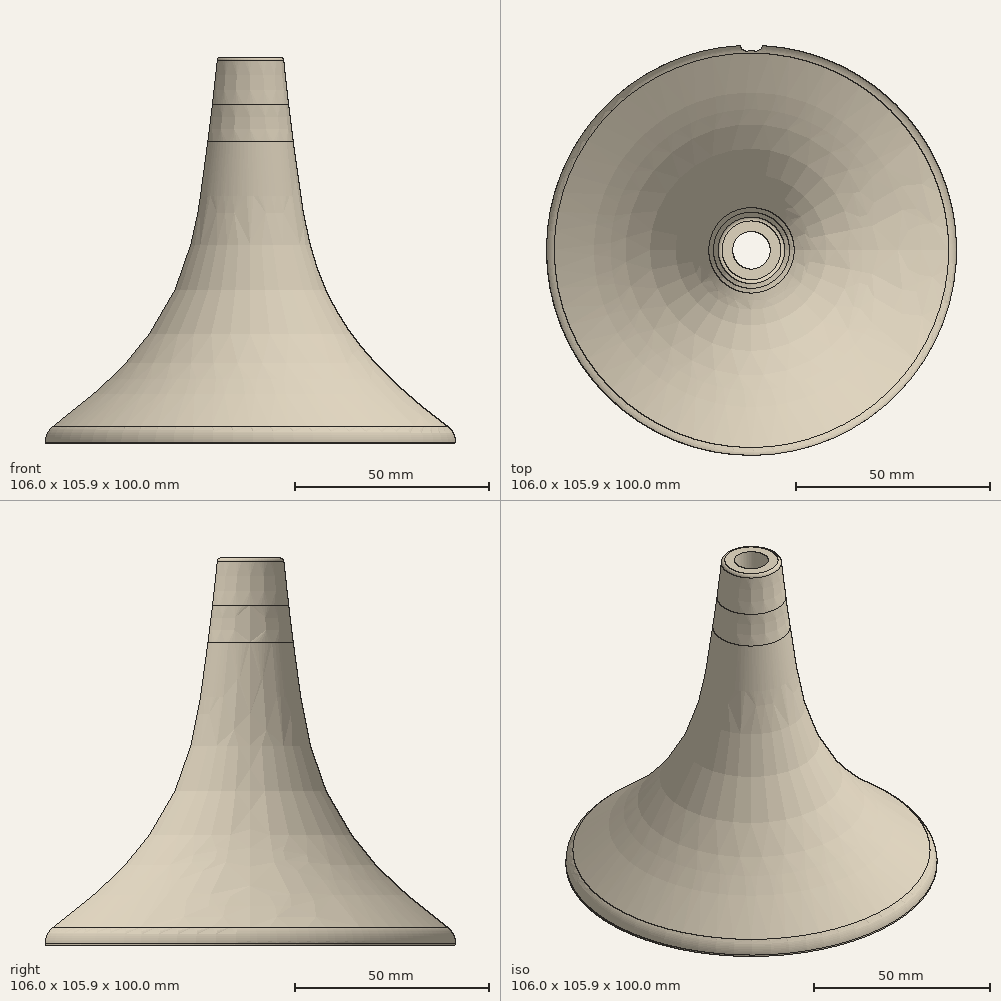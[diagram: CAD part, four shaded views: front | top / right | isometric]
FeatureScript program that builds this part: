
annotation { "Feature Type Name" : "Feature", "Feature Type Description" : "" }
export const myFeature = defineFeature(function(context is Context, id is Id, definition is map)
    precondition{}
    {
        {
            var Q0;
            Q0=qCreatedBy(makeId("Front.planeOp"),FACE);
            var sketch = newSketch(context, id + "F0", { "sketchPlane" : qUnion([Q0])});
            skLineSegment(sketch, "E0", {"start": v(30, 0) * mm, "end": v(53, 0) * mm});
            skLineSegment(sketch, "E1", {"start": v(0, 80) * mm, "end": v(0, 100) * mm});
            skLineSegment(sketch, "E2", {"start": v(0, 100) * mm, "end": v(8.5, 100) * mm});
            skLineSegment(sketch, "E3", {"start": v(53, 0) * mm, "end": v(53, 0.47) * mm});
            skFitSpline(sketch, "E4", {"points": [v(8.5, 100) * mm, v(53, 5) * mm], "startDerivative": vector(15.68, -147.82) * mm, "endDerivative": vector(109.79, -86.97) * mm});
            skArc(sketch, "E5", {"start": v(11.04, 78.1) * mm, "mid": v(14.01, 83.4) * mm, "end": v(9.83, 87.83) * mm});
            skLineSegment(sketch, "E6", {"start": v(0, 100) * mm, "end": v(0, 80) * mm});
            skLineSegment(sketch, "E7", {"start": v(0, 80) * mm, "end": v(5, 80) * mm});
            skLineSegment(sketch, "E8", {"start": v(30, 0) * mm, "end": v(30, 18) * mm});
            skLineSegment(sketch, "E9", {"start": v(0, 0) * mm, "end": v(0, 111.85) * mm, "construction": true});
            skFitSpline(sketch, "E10", {"points": [v(5, 80) * mm, v(30, 18) * mm], "startDerivative": vector(14.52, -64.25) * mm, "endDerivative": vector(57.46, -51.72) * mm});
            skFitSpline(sketch, "E11", {"points": [v(11.04, 78.1) * mm, v(53, 3) * mm], "startDerivative": vector(11.79, -91.59) * mm, "endDerivative": vector(109.3, -79.4) * mm});
            skArc(sketch, "E12.filletArc", {"start": v(53, 0.47) * mm, "mid": v(52.47, 2.71) * mm, "end": v(50.99, 4.48) * mm});
            skSolve(sketch);
        }
        {
            var Q0;
            Q0=makeQuery(id+"F0.imprint","IMPRINT",FACE,{"disambiguationData":[TD([[makeQuery(id+"F0.imprint","IMPRINT",EDGE,{"derivedFrom":sQuery(id+"F0.wireOp",EDGE,"E0")}),1.0]])]});
            var Q1;
            Q1=sQuery(id+"F0.wireOp",EDGE,"E1");
            revolve(context, id + "F1", {"surfaceOperationType" : NewSurfaceOperationType.NEW, "entities" : qUnion([Q0]), "axis" : qUnion([Q1]), "revolveType" : RevolveType.FULL});
        }
        {
            var Q0;
            Q0=makeQuery(id+"F1.opRevolve","SWEPT_EDGE",EDGE,{"disambiguationData":[OSD([sQuery(id+"F0.wireOp",EDGE,"E2"),sQuery(id+"F0.wireOp",EDGE,"E4")])]});
            fillet(context, id + "F2", {"entities" : qUnion([Q0]), "radius" : 1 * mm, "tangentPropagation" : true, "allowEdgeOverflow" : false});
        }
        {
            var Q0;
            Q0=makeQuery(id+"F1.opRevolve","SWEPT_FACE",FACE,{"disambiguationData":[OSD([sQuery(id+"F0.wireOp",EDGE,"E2")])]});
            var sketch = newSketch(context, id + "F3", { "sketchPlane" : qUnion([Q0])});
            skCircle(sketch, "E13", {"center": v(0, 0) * mm, "radius": 4.85 * mm});
            skSolve(sketch);
        }
        {
            var Q0;
            Q0=makeQuery(id+"F3.imprint","IMPRINT",FACE,{"disambiguationData":[TD([[makeQuery(id+"F3.imprint","IMPRINT",EDGE,{"derivedFrom":sQuery(id+"F3.wireOp",EDGE,"E13")}),1.0]])]});
            extrude(context, id + "F4", {"entities" : qUnion([Q0]), "operationType" : NewBodyOperationType.REMOVE, "oppositeDirection" : true, "depth" : 25 * mm, "offsetDistance" : 25 * mm});
        }
        {
            var Q0;
            Q0=qCreatedBy(makeId("Front.planeOp"),FACE);
            var sketch = newSketch(context, id + "F5", { "sketchPlane" : qUnion([Q0])});
            skLineSegment(sketch, "E14", {"start": v(0, 0) * mm, "end": v(-2.75, 0) * mm});
            skLineSegment(sketch, "E15", {"start": v(-2.75, 0) * mm, "end": v(-2.75, 4) * mm});
            skLineSegment(sketch, "E16", {"start": v(-2.75, 4) * mm, "end": v(0, 4) * mm});
            skLineSegment(sketch, "E17.MirrorCS", {"start": v(0, 0) * mm, "end": v(2.75, 0) * mm});
            skLineSegment(sketch, "E18.MirrorCS", {"start": v(2.75, 0) * mm, "end": v(2.75, 4) * mm});
            skLineSegment(sketch, "E19.MirrorCS", {"start": v(2.75, 4) * mm, "end": v(0, 4) * mm});
            skSolve(sketch);
        }
        {
            var Q0;
            Q0=makeQuery(id+"F5.imprint","IMPRINT",FACE,{"disambiguationData":[TD([[makeQuery(id+"F5.imprint","IMPRINT",EDGE,{"derivedFrom":sQuery(id+"F5.wireOp",EDGE,"E14")}),-1.0]])]});
            extrude(context, id + "F6", {"entities" : qUnion([Q0]), "operationType" : NewBodyOperationType.REMOVE, "oppositeDirection" : true, "depth" : 55 * mm, "offsetDistance" : 25 * mm});
        }
        {
            var Q0;
            Q0=makeQuery(id+"F6.boolean.opBoolean","COPY",EDGE,{"derivedFrom":makeQuery(id+"F6.opExtrude","SWEPT_EDGE",EDGE,{"disambiguationData":[OSD([sQuery(id+"F5.wireOp",EDGE,"E18.MirrorCS"),sQuery(id+"F5.wireOp",EDGE,"E19.MirrorCS")])]})});
            var Q1;
            Q1=makeQuery(id+"F6.boolean.opBoolean","COPY",EDGE,{"derivedFrom":makeQuery(id+"F6.opExtrude","SWEPT_EDGE",EDGE,{"disambiguationData":[OSD([sQuery(id+"F5.wireOp",EDGE,"E15"),sQuery(id+"F5.wireOp",EDGE,"E16")])]})});
            fillet(context, id + "F7", {"entities" : qUnion([Q0, Q1]), "radius" : 1.5 * mm, "tangentPropagation" : true, "allowEdgeOverflow" : false});
        }
        {
            var Q0;
            Q0=makeQuery(id+"F6.boolean.opBoolean","INTERSECT",EDGE,{"derivedFrom":[makeQuery(id+"F1.opRevolve","SWEPT_FACE",FACE,{"disambiguationData":[OSD([sQuery(id+"F0.wireOp",EDGE,"E8")])]}),makeQuery(id+"F6.opExtrude","SWEPT_FACE",FACE,{"disambiguationData":[OSD([sQuery(id+"F5.wireOp",EDGE,"E16"),sQuery(id+"F5.wireOp",EDGE,"E19.MirrorCS")])]})]});
            fillet(context, id + "F8", {"entities" : qUnion([Q0]), "radius" : 5 * mm, "tangentPropagation" : true, "allowEdgeOverflow" : false});
        }
        {
            var Q0;
            Q0=makeQuery(id+"F1.opRevolve","SWEPT_FACE",FACE,{"disambiguationData":[OSD([sQuery(id+"F0.wireOp",EDGE,"E0")])]});
            var sketch = newSketch(context, id + "F9", { "sketchPlane" : qUnion([Q0])});
            skCircle(sketch, "E20", {"center": v(24.75, 24.75) * mm, "radius": 1.25 * mm});
            skCircle(sketch, "E21.1.0", {"center": v(-24.75, 24.75) * mm, "radius": 1.25 * mm});
            skCircle(sketch, "E21.2.0", {"center": v(-24.75, -24.75) * mm, "radius": 1.25 * mm});
            skPoint(sketch, "E21.center", {"position": v(0, 0) * mm});
            skCircle(sketch, "E22.1.3.0", {"center": v(24.75, -24.75) * mm, "radius": 1.25 * mm});
            skSolve(sketch);
        }
        {
            var Q0;
            Q0=makeQuery(id+"F9.imprint","IMPRINT",FACE,{"disambiguationData":[TD([[makeQuery(id+"F9.imprint","IMPRINT",EDGE,{"derivedFrom":sQuery(id+"F9.wireOp",EDGE,"E21.1.0")}),1.0]])]});
            var Q1;
            Q1=makeQuery(id+"F9.imprint","IMPRINT",FACE,{"disambiguationData":[TD([[makeQuery(id+"F9.imprint","IMPRINT",EDGE,{"derivedFrom":sQuery(id+"F9.wireOp",EDGE,"E20")}),1.0]])]});
            var Q2;
            Q2=makeQuery(id+"F9.imprint","IMPRINT",FACE,{"disambiguationData":[TD([[makeQuery(id+"F9.imprint","IMPRINT",EDGE,{"derivedFrom":sQuery(id+"F9.wireOp",EDGE,"E22.1.3.0")}),1.0]])]});
            var Q3;
            Q3=makeQuery(id+"F9.imprint","IMPRINT",FACE,{"disambiguationData":[TD([[makeQuery(id+"F9.imprint","IMPRINT",EDGE,{"derivedFrom":sQuery(id+"F9.wireOp",EDGE,"E21.2.0")}),1.0]])]});
            extrude(context, id + "F10", {"entities" : qUnion([Q0, Q1, Q2, Q3]), "operationType" : NewBodyOperationType.REMOVE, "oppositeDirection" : true, "depth" : 16 * mm, "offsetDistance" : 25 * mm});
        }
        {
            var Q0;
            Q0=makeQuery(id+"F1.opRevolve","SWEPT_FACE",FACE,{"disambiguationData":[OSD([sQuery(id+"F0.wireOp",EDGE,"E0")])]});
            var sketch = newSketch(context, id + "F11", { "sketchPlane" : qUnion([Q0])});
            skCircle(sketch, "E23.0", {"center": v(24.75, 24.75) * mm, "radius": 1.25 * mm});
            skCircle(sketch, "E24", {"center": v(30.05, 30.05) * mm, "radius": 4.05 * mm});
            skCircle(sketch, "E25.1.0", {"center": v(-30.05, 30.05) * mm, "radius": 4.05 * mm});
            skCircle(sketch, "E25.2.0", {"center": v(-30.05, -30.05) * mm, "radius": 4.05 * mm});
            skPoint(sketch, "E25.center", {"position": v(0, 0) * mm});
            skCircle(sketch, "E26.1.3.0", {"center": v(30.05, -30.05) * mm, "radius": 4.05 * mm});
            skSolve(sketch);
        }
        {
            var Q0;
            Q0=makeQuery(id+"F11.imprint","IMPRINT",FACE,{"disambiguationData":[TD([[makeQuery(id+"F11.imprint","IMPRINT",EDGE,{"derivedFrom":sQuery(id+"F11.wireOp",EDGE,"E25.1.0")}),1.0]])]});
            var Q1;
            Q1=makeQuery(id+"F11.imprint","IMPRINT",FACE,{"disambiguationData":[TD([[makeQuery(id+"F11.imprint","IMPRINT",EDGE,{"derivedFrom":sQuery(id+"F11.wireOp",EDGE,"E24")}),1.0]])]});
            var Q2;
            Q2=makeQuery(id+"F11.imprint","IMPRINT",FACE,{"disambiguationData":[TD([[makeQuery(id+"F11.imprint","IMPRINT",EDGE,{"derivedFrom":sQuery(id+"F11.wireOp",EDGE,"E26.1.3.0")}),1.0]])]});
            var Q3;
            Q3=makeQuery(id+"F11.imprint","IMPRINT",FACE,{"disambiguationData":[TD([[makeQuery(id+"F11.imprint","IMPRINT",EDGE,{"derivedFrom":sQuery(id+"F11.wireOp",EDGE,"E25.2.0")}),1.0]])]});
            extrude(context, id + "F12", {"entities" : qUnion([Q0, Q1, Q2, Q3]), "operationType" : NewBodyOperationType.REMOVE, "oppositeDirection" : true, "depth" : 1.2 * mm, "offsetDistance" : 25 * mm});
        }
    });
